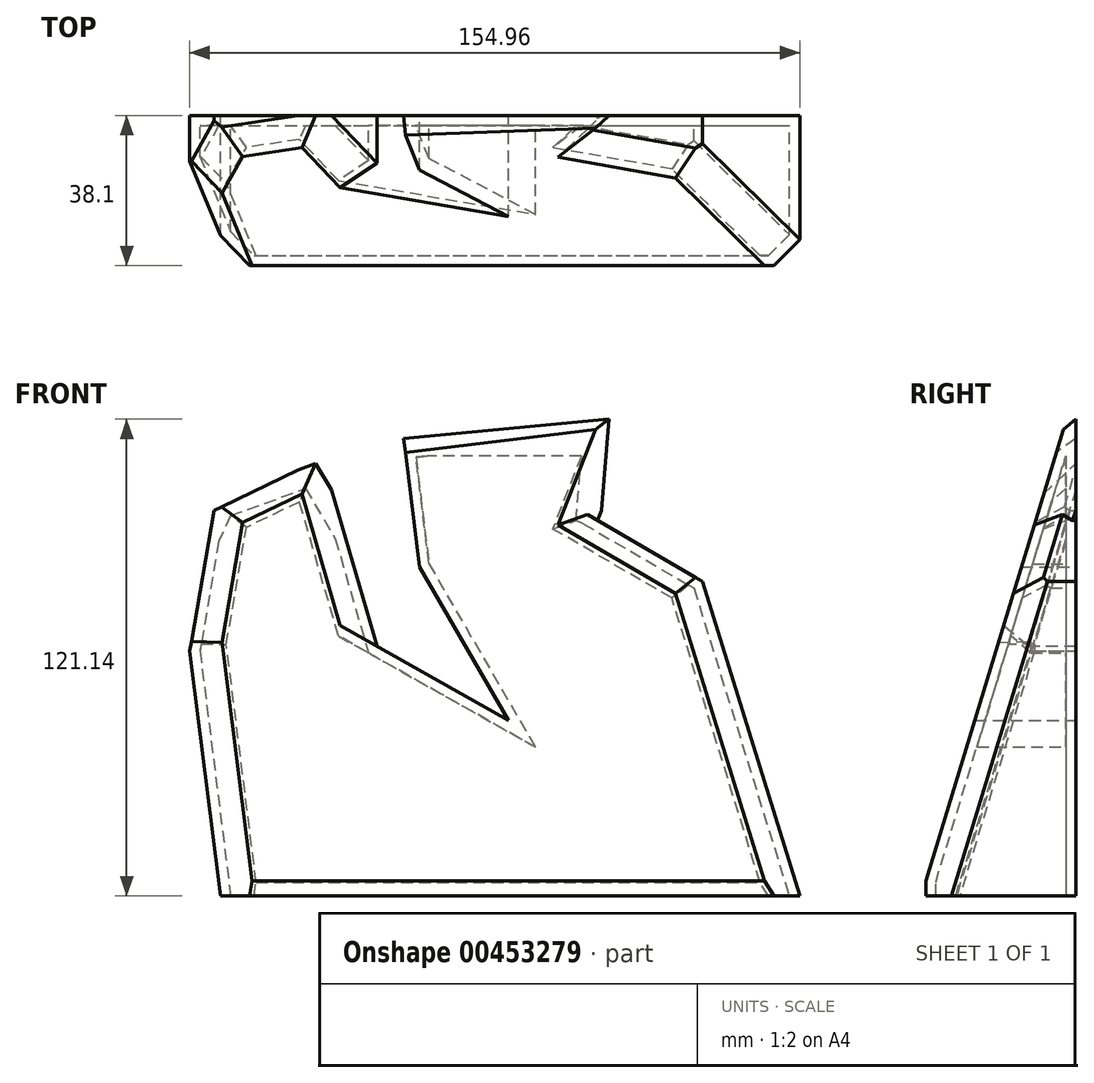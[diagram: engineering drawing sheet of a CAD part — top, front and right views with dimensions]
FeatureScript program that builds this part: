
annotation { "Feature Type Name" : "Feature", "Feature Type Description" : "" }
export const myFeature = defineFeature(function(context is Context, id is Id, definition is map)
    precondition{}
    {
        {
            var Q0;
            Q0=qCreatedBy(makeId("Front.planeOp"),FACE);
            var sketch = newSketch(context, id + "F0", { "sketchPlane" : qUnion([Q0])});
            skLineSegment(sketch, "E0", {"start": v(-75.65, -25.31) * mm, "end": v(71.5, -25.31) * mm});
            skLineSegment(sketch, "E1", {"start": v(20.15, 70.06) * mm, "end": v(32.16, 100.52) * mm});
            skLineSegment(sketch, "E2", {"start": v(32.16, 100.52) * mm, "end": v(-29.4, 93.04) * mm});
            skLineSegment(sketch, "E3", {"start": v(-77.35, 72.63) * mm, "end": v(-83.47, 36.92) * mm});
            skLineSegment(sketch, "E4", {"start": v(-83.47, 36.92) * mm, "end": v(-75.65, -25.31) * mm});
            skLineSegment(sketch, "E5", {"start": v(-77.35, 72.63) * mm, "end": v(-49.8, 85.9) * mm});
            skLineSegment(sketch, "E6", {"start": v(-49.8, 85.9) * mm, "end": v(-35.93, 38.13) * mm});
            skLineSegment(sketch, "E7", {"start": v(20.15, 70.06) * mm, "end": v(46.73, 54.59) * mm});
            skLineSegment(sketch, "E8", {"start": v(46.73, 54.59) * mm, "end": v(71.5, -25.31) * mm});
            skLineSegment(sketch, "E9", {"start": v(-29.4, 93.04) * mm, "end": v(-25.16, 58.2) * mm});
            skLineSegment(sketch, "E10", {"start": v(-25.16, 58.2) * mm, "end": v(-2.56, 19.3) * mm});
            skLineSegment(sketch, "E11", {"start": v(-2.56, 19.3) * mm, "end": v(-35.93, 38.13) * mm});
            skSolve(sketch);
        }
        {
            var Q0;
            Q0=qSketchRegion(id+"F0",true);
            extrude(context, id + "F1", {"entities" : qUnion([Q0]), "depth" : 38.1 * mm});
        }
        {
            var Q0;
            Q0=qCreatedBy(makeId("Right.planeOp"),FACE);
            cPlane(context, id + "F2", {"entities" : qUnion([Q0]), "cplaneType" : CPlaneType.OFFSET, "offset" : 76.2 * mm, "width" : 152.4 * mm, "height" : 152.4 * mm});
        }
        {
            var Q0;
            Q0=qCreatedBy(id+"F2.planeOp",FACE);
            var sketch = newSketch(context, id + "F3", { "sketchPlane" : qUnion([Q0])});
            skLineSegment(sketch, "E12", {"start": v(-38.62, -23.16) * mm, "end": v(0, 103.45) * mm});
            skLineSegment(sketch, "E13", {"start": v(0, 103.45) * mm, "end": v(-41.99, 103.45) * mm});
            skLineSegment(sketch, "E14", {"start": v(-41.99, 103.45) * mm, "end": v(-38.62, -23.16) * mm});
            skSolve(sketch);
        }
        {
            var Q0;
            Q0=qSketchRegion(id+"F3",true);
            extrude(context, id + "F4", {"entities" : qUnion([Q0]), "operationType" : NewBodyOperationType.REMOVE, "endBound" : BoundingType.THROUGH_ALL, "oppositeDirection" : true, "depth" : 25.4 * mm});
        }
        {
            var Q0;
            Q0=makeQuery(id+"F4.boolean.opBoolean","INTERSECT",EDGE,{"derivedFrom":[makeQuery(id+"F1.opExtrude","SWEPT_FACE",FACE,{"disambiguationData":[OSD([sQuery(id+"F0.wireOp",EDGE,"E5")])]}),makeQuery(id+"F4.opExtrude","SWEPT_FACE",FACE,{"disambiguationData":[OSD([sQuery(id+"F3.wireOp",EDGE,"E12")])]})]});
            var Q1;
            Q1=makeQuery(id+"F4.boolean.opBoolean","INTERSECT",EDGE,{"derivedFrom":[makeQuery(id+"F1.opExtrude","SWEPT_FACE",FACE,{"disambiguationData":[OSD([sQuery(id+"F0.wireOp",EDGE,"E6")])]}),makeQuery(id+"F4.opExtrude","SWEPT_FACE",FACE,{"disambiguationData":[OSD([sQuery(id+"F3.wireOp",EDGE,"E12")])]})]});
            var Q2;
            Q2=makeQuery(id+"F4.boolean.opBoolean","INTERSECT",EDGE,{"derivedFrom":[makeQuery(id+"F1.opExtrude","SWEPT_FACE",FACE,{"disambiguationData":[OSD([sQuery(id+"F0.wireOp",EDGE,"6o2LRsBb-Jyn4-08lC-5Gxt-SUnK0TZeSw5C")])]}),makeQuery(id+"F4.opExtrude","SWEPT_FACE",FACE,{"disambiguationData":[OSD([sQuery(id+"F3.wireOp",EDGE,"E12")])]})]});
            var Q3;
            Q3=makeQuery(id+"F4.boolean.opBoolean","INTERSECT",EDGE,{"derivedFrom":[makeQuery(id+"F1.opExtrude","SWEPT_FACE",FACE,{"disambiguationData":[OSD([sQuery(id+"F0.wireOp",EDGE,"E2")])]}),makeQuery(id+"F4.opExtrude","SWEPT_FACE",FACE,{"disambiguationData":[OSD([sQuery(id+"F3.wireOp",EDGE,"E12")])]})]});
            var Q4;
            Q4=makeQuery(id+"F4.boolean.opBoolean","INTERSECT",EDGE,{"derivedFrom":[makeQuery(id+"F1.opExtrude","SWEPT_FACE",FACE,{"disambiguationData":[OSD([sQuery(id+"F0.wireOp",EDGE,"E1")])]}),makeQuery(id+"F4.opExtrude","SWEPT_FACE",FACE,{"disambiguationData":[OSD([sQuery(id+"F3.wireOp",EDGE,"E12")])]})]});
            var Q5;
            Q5=makeQuery(id+"F4.boolean.opBoolean","INTERSECT",EDGE,{"derivedFrom":[makeQuery(id+"F1.opExtrude","SWEPT_FACE",FACE,{"disambiguationData":[OSD([sQuery(id+"F0.wireOp",EDGE,"E7")])]}),makeQuery(id+"F4.opExtrude","SWEPT_FACE",FACE,{"disambiguationData":[OSD([sQuery(id+"F3.wireOp",EDGE,"E12")])]})]});
            var Q6;
            Q6=makeQuery(id+"F4.boolean.opBoolean","INTERSECT",EDGE,{"derivedFrom":[makeQuery(id+"F1.opExtrude","SWEPT_FACE",FACE,{"disambiguationData":[OSD([sQuery(id+"F0.wireOp",EDGE,"E8")])]}),makeQuery(id+"F4.opExtrude","SWEPT_FACE",FACE,{"disambiguationData":[OSD([sQuery(id+"F3.wireOp",EDGE,"E12")])]})]});
            var Q7;
            Q7=makeQuery(id+"F4.boolean.opBoolean","INTERSECT",EDGE,{"derivedFrom":[makeQuery(id+"F1.opExtrude","SWEPT_FACE",FACE,{"disambiguationData":[OSD([sQuery(id+"F0.wireOp",EDGE,"E4")])]}),makeQuery(id+"F4.opExtrude","SWEPT_FACE",FACE,{"disambiguationData":[OSD([sQuery(id+"F3.wireOp",EDGE,"E12")])]})]});
            var Q8;
            Q8=makeQuery(id+"F4.boolean.opBoolean","INTERSECT",EDGE,{"derivedFrom":[makeQuery(id+"F1.opExtrude","SWEPT_FACE",FACE,{"disambiguationData":[OSD([sQuery(id+"F0.wireOp",EDGE,"E3")])]}),makeQuery(id+"F4.opExtrude","SWEPT_FACE",FACE,{"disambiguationData":[OSD([sQuery(id+"F3.wireOp",EDGE,"E12")])]})]});
            chamfer(context, id + "F5", {"entities" : qUnion([Q0, Q1, Q2, Q3, Q4, Q5, Q6, Q7, Q8]), "width" : 8.13 * mm, "tangentPropagation" : true});
        }
        {
            var Q0;
            Q0=makeQuery(id+"F1.opExtrude","SWEPT_FACE",FACE,{"disambiguationData":[OSD([sQuery(id+"F0.wireOp",EDGE,"E0")])]});
            shell(context, id + "F6", {"entities" : qUnion([Q0]), "thickness" : 2.54 * mm});
        }
    });
